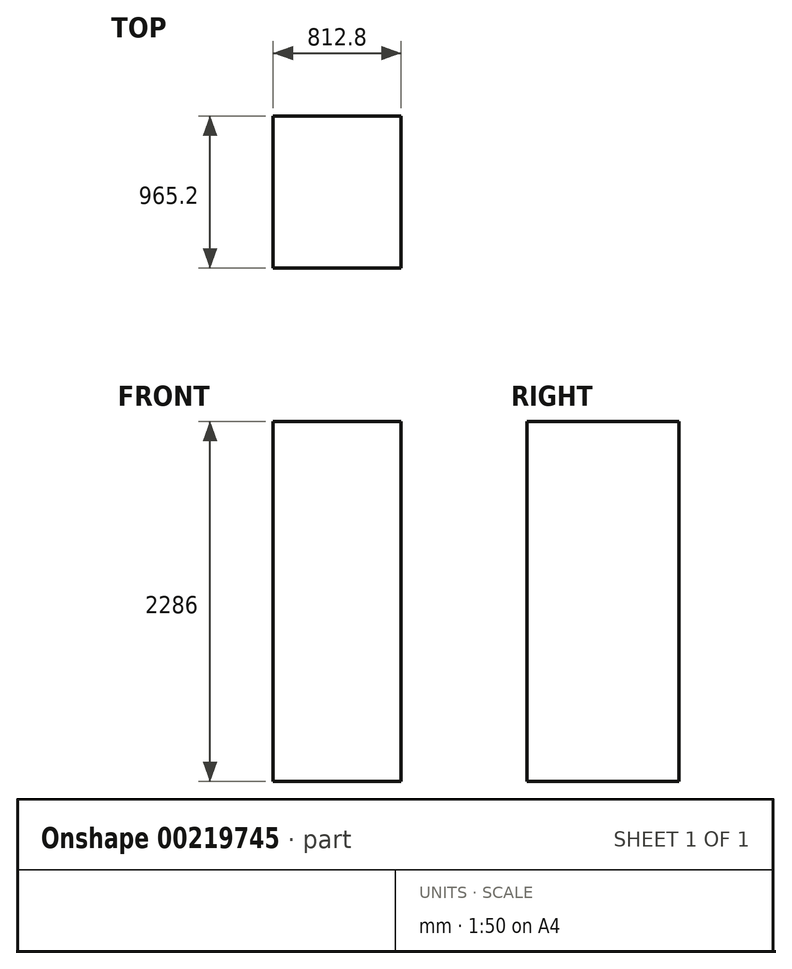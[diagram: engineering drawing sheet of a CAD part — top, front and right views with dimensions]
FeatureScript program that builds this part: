
annotation { "Feature Type Name" : "Feature", "Feature Type Description" : "" }
export const myFeature = defineFeature(function(context is Context, id is Id, definition is map)
    precondition{}
    {
        {
            var Q0;
            Q0=qCreatedBy(makeId("Front.planeOp"),FACE);
            var sketch = newSketch(context, id + "F0", { "sketchPlane" : qUnion([Q0])});
            skLineSegment(sketch, "E0.bottom", {"start": v(0, 0) * mm, "end": v(-812.8, 0) * mm});
            skLineSegment(sketch, "E0.top", {"start": v(0, 2286) * mm, "end": v(-812.8, 2286) * mm});
            skLineSegment(sketch, "E0.left", {"start": v(0, 0) * mm, "end": v(0, 2286) * mm});
            skLineSegment(sketch, "E0.right", {"start": v(-812.8, 0) * mm, "end": v(-812.8, 2286) * mm});
            skSolve(sketch);
        }
        {
            var Q0;
            Q0=makeQuery(id+"F0.imprint","IMPRINT",FACE,{"disambiguationData":[TD([[makeQuery(id+"F0.imprint","IMPRINT",EDGE,{"derivedFrom":sQuery(id+"F0.wireOp",EDGE,"E0.bottom")}),-1.0]])]});
            extrude(context, id + "F1", {"entities" : qUnion([Q0]), "oppositeDirection" : true, "depth" : 965.2 * mm});
        }
    });
